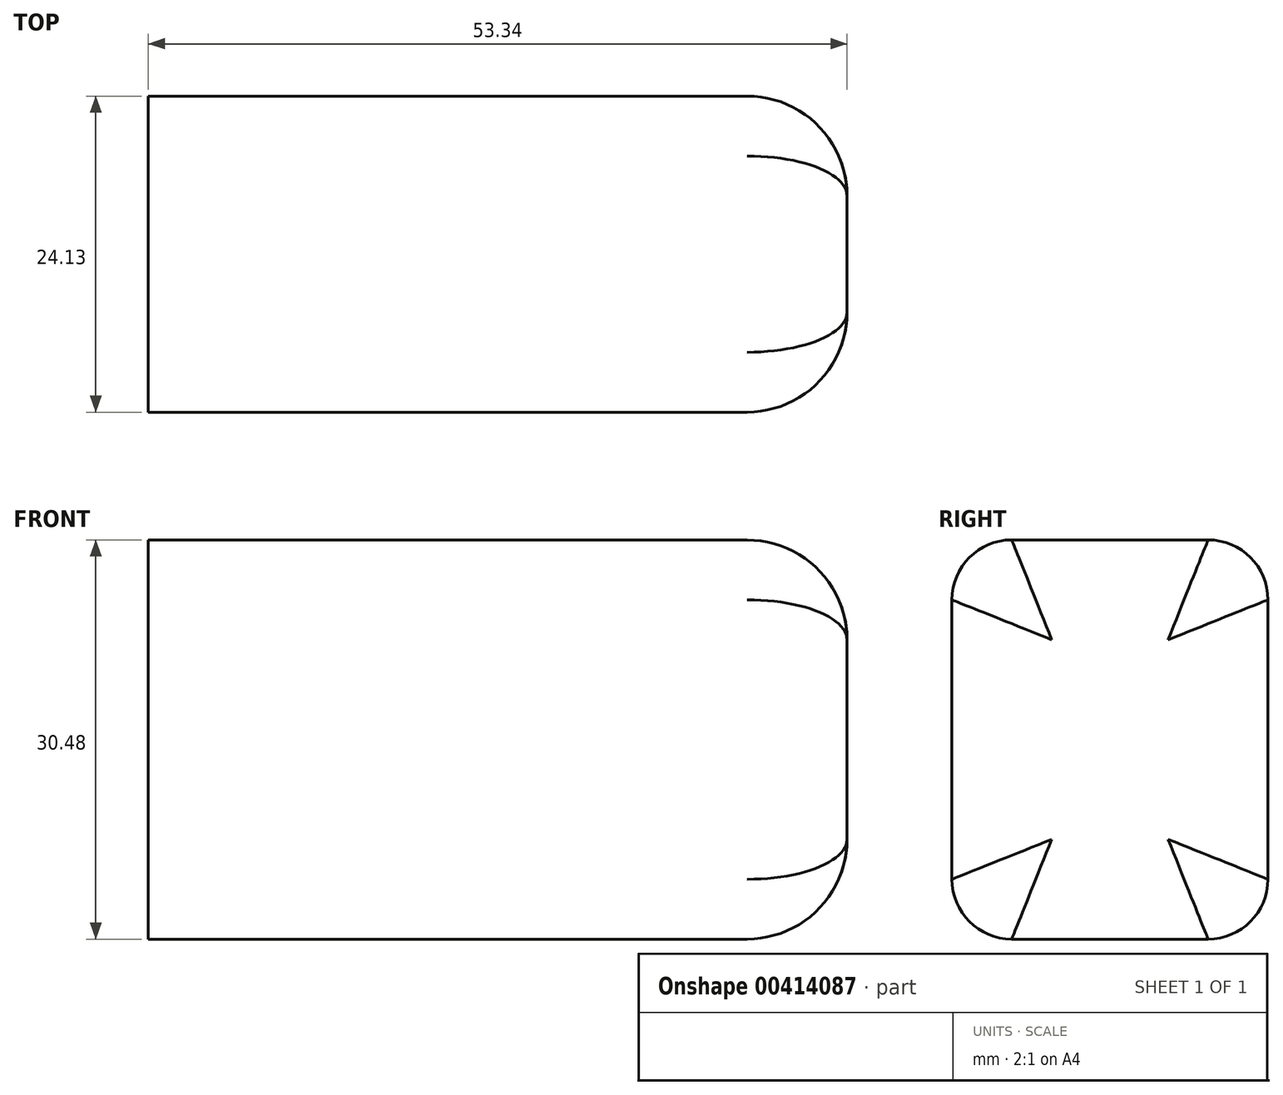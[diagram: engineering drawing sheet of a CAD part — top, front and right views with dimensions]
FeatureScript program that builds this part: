
annotation { "Feature Type Name" : "Feature", "Feature Type Description" : "" }
export const myFeature = defineFeature(function(context is Context, id is Id, definition is map)
    precondition{}
    {
        {
            var Q0;
            Q0=qCreatedBy(makeId("Front.planeOp"),FACE);
            var sketch = newSketch(context, id + "F0", { "sketchPlane" : qUnion([Q0])});
            skLineSegment(sketch, "E0.bottom", {"start": v(-21.3, -2.77) * mm, "end": v(32.04, -2.77) * mm});
            skLineSegment(sketch, "E0.top", {"start": v(-21.3, -33.25) * mm, "end": v(32.04, -33.25) * mm});
            skLineSegment(sketch, "E0.left", {"start": v(-21.3, -2.77) * mm, "end": v(-21.3, -33.25) * mm});
            skLineSegment(sketch, "E0.right", {"start": v(32.04, -2.77) * mm, "end": v(32.04, -33.25) * mm});
            skSolve(sketch);
        }
        {
            var Q0;
            Q0=makeQuery(id+"F0.imprint","IMPRINT",FACE,{"disambiguationData":[TD([[makeQuery(id+"F0.imprint","IMPRINT",EDGE,{"derivedFrom":sQuery(id+"F0.wireOp",EDGE,"E0.bottom")}),-1.0]])]});
            extrude(context, id + "F1", {"entities" : qUnion([Q0]), "depth" : 24.13 * mm});
        }
        {
            var Q0;
            Q0=makeQuery(id+"F1.opExtrude","CAP_EDGE",EDGE,{"disambiguationData":[OSD([sQuery(id+"F0.wireOp",EDGE,"E0.bottom")])],"isStart":false});
            var Q1;
            Q1=makeQuery(id+"F1.opExtrude","CAP_EDGE",EDGE,{"disambiguationData":[OSD([sQuery(id+"F0.wireOp",EDGE,"E0.top")])],"isStart":false});
            var Q2;
            Q2=makeQuery(id+"F1.opExtrude","CAP_EDGE",EDGE,{"disambiguationData":[OSD([sQuery(id+"F0.wireOp",EDGE,"E0.top")])],"isStart":true});
            var Q3;
            Q3=makeQuery(id+"F1.opExtrude","CAP_EDGE",EDGE,{"disambiguationData":[OSD([sQuery(id+"F0.wireOp",EDGE,"E0.bottom")])],"isStart":true});
            fillet(context, id + "F2", {"entities" : qUnion([Q0, Q1, Q2, Q3]), "radius" : 4.57 * mm, "tangentPropagation" : true, "allowEdgeOverflow" : false});
        }
        {
            var Q0;
            Q0=makeQuery(id+"F2.opFillet","BLEND_EDGE",EDGE,{"blendedFrom":[makeQuery(id+"F1.opExtrude","CAP_EDGE",EDGE,{"disambiguationData":[OSD([sQuery(id+"F0.wireOp",EDGE,"E0.top")])],"isStart":false}),makeQuery(id+"F1.opExtrude","SWEPT_FACE",FACE,{"disambiguationData":[OSD([sQuery(id+"F0.wireOp",EDGE,"E0.right")])]})],"blendedInto":[makeQuery(id+"F1.opExtrude","SWEPT_FACE",FACE,{"disambiguationData":[OSD([sQuery(id+"F0.wireOp",EDGE,"E0.right")])]})]});
            var Q1;
            Q1=makeQuery(id+"F1.opExtrude","CAP_EDGE",EDGE,{"disambiguationData":[OSD([sQuery(id+"F0.wireOp",EDGE,"E0.right")])],"isStart":false});
            var Q2;
            Q2=makeQuery(id+"F2.opFillet","BLEND_EDGE",EDGE,{"blendedFrom":[makeQuery(id+"F1.opExtrude","CAP_EDGE",EDGE,{"disambiguationData":[OSD([sQuery(id+"F0.wireOp",EDGE,"E0.bottom")])],"isStart":false}),makeQuery(id+"F1.opExtrude","SWEPT_FACE",FACE,{"disambiguationData":[OSD([sQuery(id+"F0.wireOp",EDGE,"E0.right")])]})],"blendedInto":[makeQuery(id+"F1.opExtrude","SWEPT_FACE",FACE,{"disambiguationData":[OSD([sQuery(id+"F0.wireOp",EDGE,"E0.right")])]})]});
            var Q3;
            Q3=makeQuery(id+"F2.opFillet","BLEND_EDGE",EDGE,{"blendedFrom":[makeQuery(id+"F1.opExtrude","CAP_EDGE",EDGE,{"disambiguationData":[OSD([sQuery(id+"F0.wireOp",EDGE,"E0.bottom")])],"isStart":true}),makeQuery(id+"F1.opExtrude","SWEPT_FACE",FACE,{"disambiguationData":[OSD([sQuery(id+"F0.wireOp",EDGE,"E0.right")])]})],"blendedInto":[makeQuery(id+"F1.opExtrude","SWEPT_FACE",FACE,{"disambiguationData":[OSD([sQuery(id+"F0.wireOp",EDGE,"E0.right")])]})]});
            var Q4;
            Q4=makeQuery(id+"F1.opExtrude","CAP_EDGE",EDGE,{"disambiguationData":[OSD([sQuery(id+"F0.wireOp",EDGE,"E0.right")])],"isStart":true});
            var Q5;
            Q5=makeQuery(id+"F2.opFillet","BLEND_EDGE",EDGE,{"blendedFrom":[makeQuery(id+"F1.opExtrude","CAP_EDGE",EDGE,{"disambiguationData":[OSD([sQuery(id+"F0.wireOp",EDGE,"E0.top")])],"isStart":true}),makeQuery(id+"F1.opExtrude","SWEPT_FACE",FACE,{"disambiguationData":[OSD([sQuery(id+"F0.wireOp",EDGE,"E0.right")])]})],"blendedInto":[makeQuery(id+"F1.opExtrude","SWEPT_FACE",FACE,{"disambiguationData":[OSD([sQuery(id+"F0.wireOp",EDGE,"E0.right")])]})]});
            fillet(context, id + "F3", {"entities" : qUnion([Q0, Q1, Q2, Q3, Q4, Q5]), "radius" : 7.62 * mm, "tangentPropagation" : true, "allowEdgeOverflow" : false});
        }
    });
